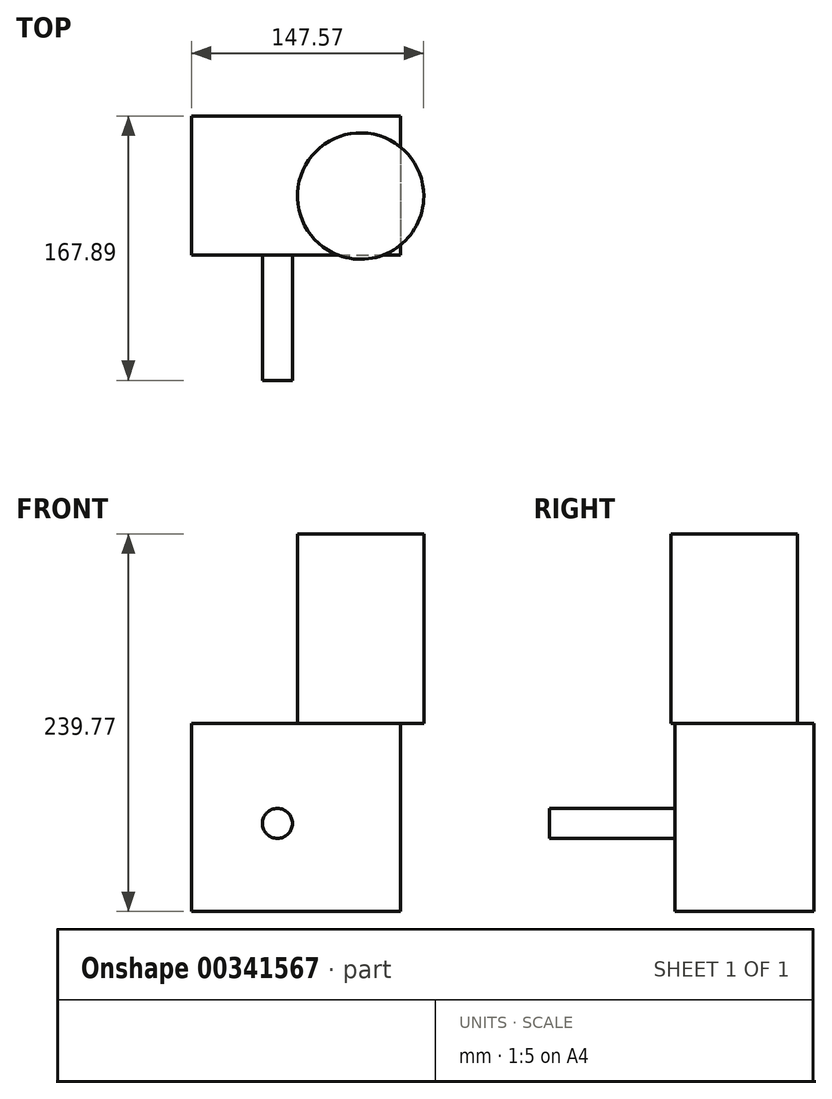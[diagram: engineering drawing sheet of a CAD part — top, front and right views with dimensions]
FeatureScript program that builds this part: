
annotation { "Feature Type Name" : "Feature", "Feature Type Description" : "" }
export const myFeature = defineFeature(function(context is Context, id is Id, definition is map)
    precondition{}
    {
        {
            var Q0;
            Q0=qCreatedBy(makeId("Front.planeOp"),FACE);
            var sketch = newSketch(context, id + "F0", { "sketchPlane" : qUnion([Q0])});
            skLineSegment(sketch, "E0.bottom", {"start": v(-67.33, 65.2) * mm, "end": v(65.51, 65.2) * mm});
            skLineSegment(sketch, "E0.top", {"start": v(-67.33, -54.17) * mm, "end": v(65.51, -54.17) * mm});
            skLineSegment(sketch, "E0.left", {"start": v(-67.33, 65.2) * mm, "end": v(-67.33, -54.17) * mm});
            skLineSegment(sketch, "E0.right", {"start": v(65.51, 65.2) * mm, "end": v(65.51, -54.17) * mm});
            skSolve(sketch);
        }
        {
            var Q0;
            Q0 = qSketchRegion(id + "F0", true);
            extrude(context, id + "F1", {"entities" : qUnion([Q0]), "oppositeDirection" : true, "depth" : 88.4 * mm});
        }
        {
            var Q0;
            Q0=makeQuery(id+"F1.opExtrude","SWEPT_FACE",FACE,{"disambiguationData":[OSD([sQuery(id+"F0.wireOp",EDGE,"E0.bottom")])]});
            var sketch = newSketch(context, id + "F2", { "sketchPlane" : qUnion([Q0])});
            skCircle(sketch, "E1", {"center": v(40.11, 37.6) * mm, "radius": 40.13 * mm});
            skSolve(sketch);
        }
        {
            var Q0;
            Q0 = qSketchRegion(id + "F2", true);
            extrude(context, id + "F3", {"entities" : qUnion([Q0]), "operationType" : NewBodyOperationType.ADD, "depth" : 120.4 * mm});
        }
        {
            var Q0;
            Q0=makeQuery(id+"F1.opExtrude","CAP_FACE",FACE,{"disambiguationData":[OSD([sQuery(id+"F0.wireOp",EDGE,"E0.bottom"),sQuery(id+"F0.wireOp",EDGE,"E0.top"),sQuery(id+"F0.wireOp",EDGE,"E0.left"),sQuery(id+"F0.wireOp",EDGE,"E0.right")])],"isStart":true});
            var sketch = newSketch(context, id + "F4", { "sketchPlane" : qUnion([Q0])});
            skCircle(sketch, "E2", {"center": v(-12.72, 1.7) * mm, "radius": 9.53 * mm});
            skSolve(sketch);
        }
        {
            var Q0;
            Q0 = qSketchRegion(id + "F4", true);
            extrude(context, id + "F5", {"entities" : qUnion([Q0]), "operationType" : NewBodyOperationType.ADD, "depth" : 79.5 * mm});
        }
    });
